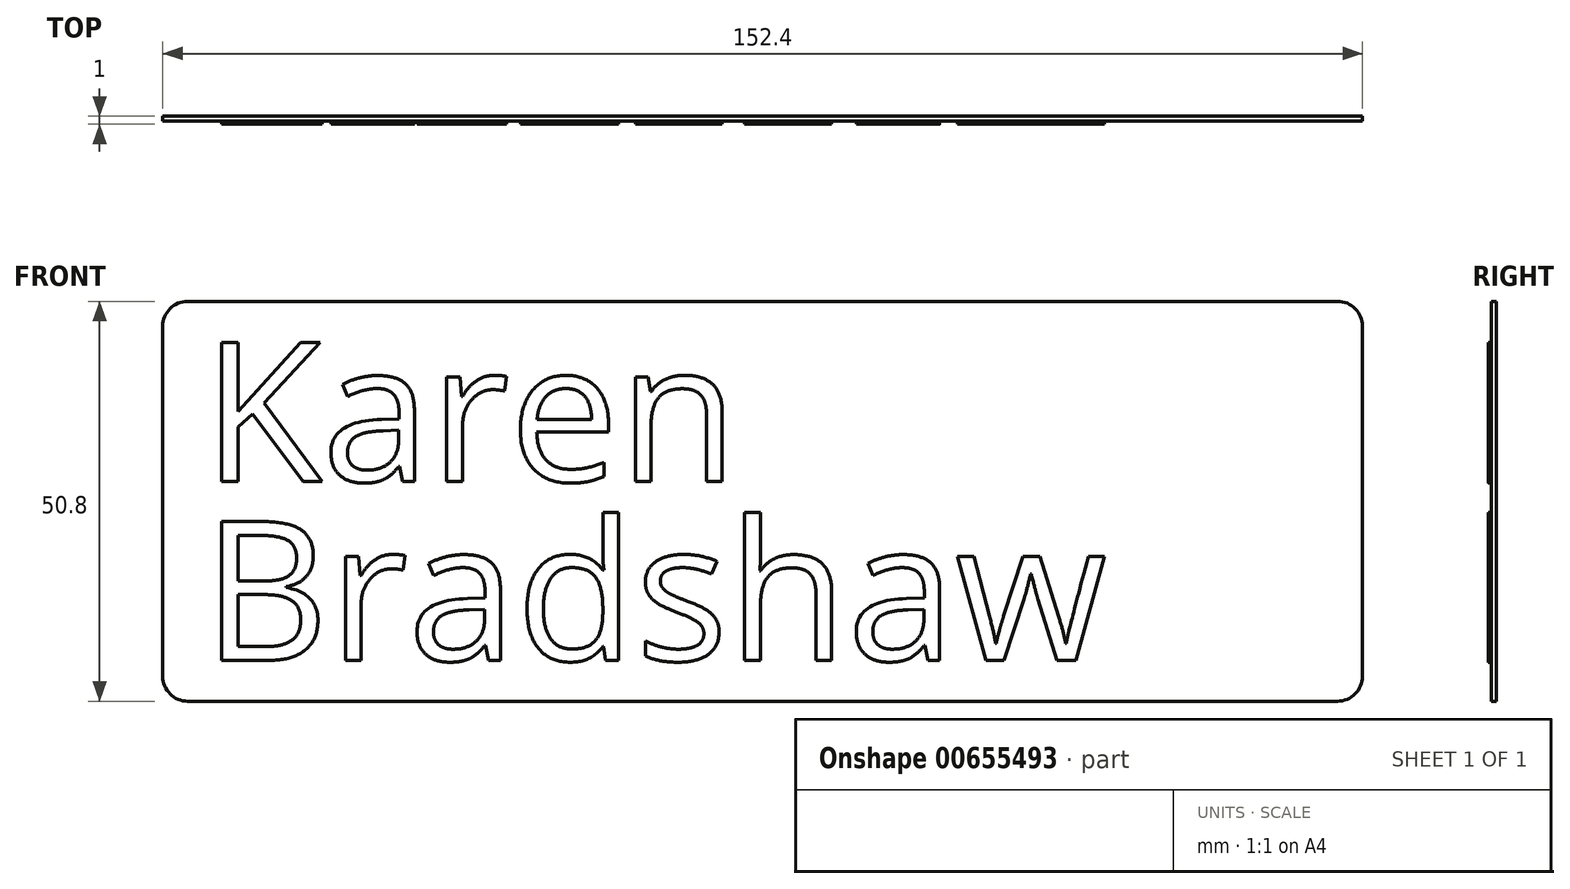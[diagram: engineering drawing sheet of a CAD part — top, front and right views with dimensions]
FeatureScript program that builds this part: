
annotation { "Feature Type Name" : "Feature", "Feature Type Description" : "" }
export const myFeature = defineFeature(function(context is Context, id is Id, definition is map)
    precondition{}
    {
        {
            var Q0;
            Q0=qCreatedBy(makeId("Front.planeOp"),FACE);
            var sketch = newSketch(context, id + "F0", { "sketchPlane" : qUnion([Q0])});
            skLineSegment(sketch, "E0.bottom", {"start": v(3.18, 0) * mm, "end": v(149.22, 0) * mm});
            skLineSegment(sketch, "E0.top", {"start": v(3.18, -50.8) * mm, "end": v(149.22, -50.8) * mm});
            skLineSegment(sketch, "E0.left", {"start": v(0, -3.17) * mm, "end": v(0, -47.63) * mm});
            skLineSegment(sketch, "E0.right", {"start": v(152.4, -3.17) * mm, "end": v(152.4, -47.63) * mm});
            skPoint(sketch, "E1.visualSharp", {"position": v(0, 0) * mm});
            skArc(sketch, "E1.filletArc", {"start": v(3.18, 0) * mm, "mid": v(0.93, -0.93) * mm, "end": v(0, -3.18) * mm});
            skPoint(sketch, "E2.visualSharp", {"position": v(152.4, 0) * mm});
            skArc(sketch, "E2.filletArc", {"start": v(152.4, -3.18) * mm, "mid": v(151.47, -0.93) * mm, "end": v(149.22, 0) * mm});
            skPoint(sketch, "E3.visualSharp", {"position": v(152.4, -50.8) * mm});
            skArc(sketch, "E3.filletArc", {"start": v(149.22, -50.8) * mm, "mid": v(151.47, -49.87) * mm, "end": v(152.4, -47.63) * mm});
            skPoint(sketch, "E4.visualSharp", {"position": v(0, -50.8) * mm});
            skArc(sketch, "E4.filletArc", {"start": v(0, -47.63) * mm, "mid": v(0.93, -49.87) * mm, "end": v(3.18, -50.8) * mm});
            skSolve(sketch);
        }
        {
            var Q0;
            Q0=qSketchRegion(id+"F0",true);
            extrude(context, id + "F1", {"entities" : qUnion([Q0]), "depth" : .6 * mm, "offsetDistance" : 25.4 * mm});
        }
        {
            var Q0;
            Q0=makeQuery(id+"F1.opExtrude","CAP_FACE",FACE,{"disambiguationData":[OSD([sQuery(id+"F0.wireOp",EDGE,"E0.bottom"),sQuery(id+"F0.wireOp",EDGE,"E0.top"),sQuery(id+"F0.wireOp",EDGE,"E0.left"),sQuery(id+"F0.wireOp",EDGE,"E0.right"),sQuery(id+"F0.wireOp",EDGE,"E1.filletArc"),sQuery(id+"F0.wireOp",EDGE,"E2.filletArc"),sQuery(id+"F0.wireOp",EDGE,"E3.filletArc"),sQuery(id+"F0.wireOp",EDGE,"E4.filletArc")])],"isStart":false});
            var sketch = newSketch(context, id + "F2", { "sketchPlane" : qUnion([Q0])});
            skText(sketch, "E5", { "text": "Karen", "fontName": "OpenSans-Regular.ttf"});
            skText(sketch, "E6", { "text": "Bradshaw", "fontName": "OpenSans-Regular.ttf"});
            const initialGuessF2  = {"E5": [0.00508, -0.02286, 1, 0, 0.01778], "E6": [0.00508, -0.04561, 1, 0, 0.01778]};
            skSetInitialGuess(sketch, initialGuessF2);
            skSolve(sketch);
        }
        {
            var Q0;
            Q0=qSketchRegion(id+"F2",true);
            extrude(context, id + "F3", {"entities" : qUnion([Q0]), "operationType" : NewBodyOperationType.ADD, "depth" : .4 * mm, "offsetDistance" : 25.4 * mm});
        }
    });
